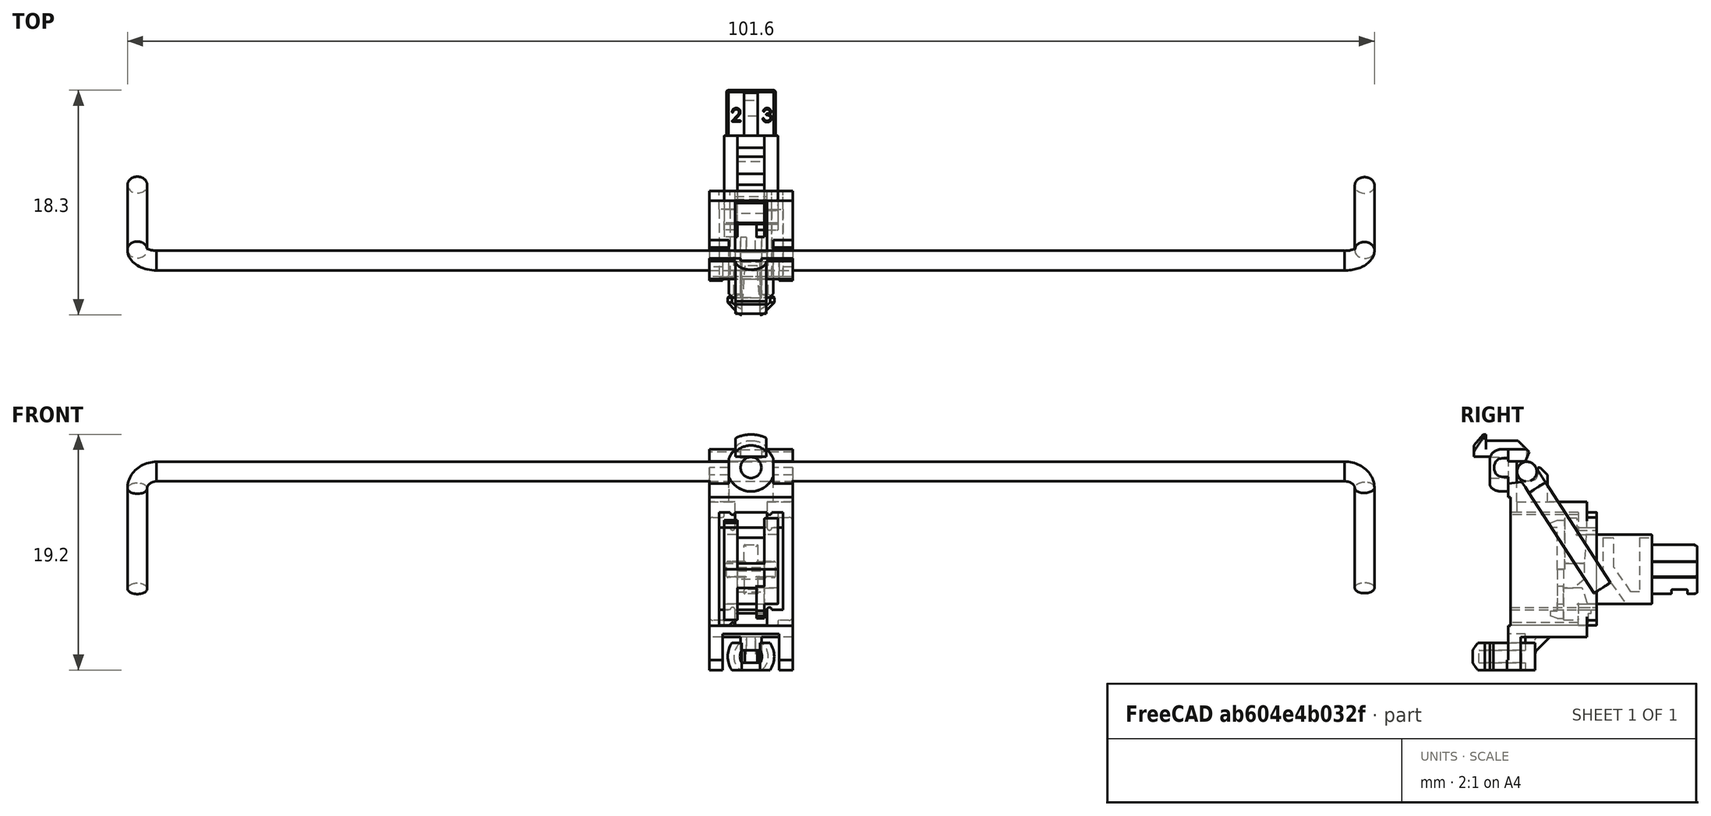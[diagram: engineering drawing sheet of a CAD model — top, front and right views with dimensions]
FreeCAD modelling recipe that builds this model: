
FCSTD DOCUMENT  (FreeCAD 0.18R16158 (Git))
Label: Stabilizer_Cherry_MX_6.25u
License: CreativeCommons Attribution-ShareAlike
LicenseURL: http://creativecommons.org/licenses/by-sa/4.0/
objects: Part::Feature×4, App::Part×3, PartDesign::Plane×2, Sketcher::SketchObject×2, PartDesign::AdditivePipe×1, PartDesign::Body×1
note: 11 computed .brp shape members not serialized (recipe doc carries the construction recipe); baked Part::Feature solids carry a one-line shape summary decoded from their .brp

FEATURE [Part::Feature] Part__Feature  label="Stabilizer_Base"
  shape: bbox 6.802 x 10.1 x 19.67 mm, 163 faces (baked)
FEATURE [Part::Feature] Part__Feature001  label="Stabilizer_Key"
  Placement = pos=(0,8.1,0) rot=(0,0,1;0rad)
  shape: bbox 4.6 x 11.96 x 8.302 mm, 299 faces (baked)
FEATURE [App::Part] Part  label="Stabilizer_End_1"
  Group = -> [Part__Feature001,Part__Feature]
  Origin = -> Origin001
  Placement = pos=(-50,0,0) rot=(0,0,1;0rad)
FEATURE [PartDesign::Plane] DatumPlane
  Length = 112.187
  MapMode = 13
  Placement = pos=(23.0333,0.289849,4.3056) rot=(1,0,0;2.14498rad)
  ResizeMode = 0
  Width = 38.2565
FEATURE [PartDesign::Plane] DatumPlane001
  Length = 38.2565
  MapMode = 11
  Placement = pos=(8e-15,4.09188,-1.57187) rot=(0.272451,-0.272451,0.92279;1.65106rad)
  ResizeMode = 0
  Width = 112.187
FEATURE [Sketcher::SketchObject] Sketch
  MapMode = 5
  Placement = pos=(8e-15,4.09188,-1.57187) rot=(0.272451,-0.272451,0.92279;1.65106rad)
  Support = -> [DatumPlane001]
  sketch-geometry (5):
    g0: Circle CenterX=0 CenterY=50 CenterZ=0 NormalX=0 NormalY=0 NormalZ=1 AngleXU=0 Radius=0.8
    g1: Circle [constr] CenterX=0 CenterY=-50 CenterZ=0 NormalX=0 NormalY=0 NormalZ=1 AngleXU=0 Radius=0.8
    g2: LineSegment [constr] StartX=0 StartY=50 StartZ=0 EndX=0 EndY=0 EndZ=0
    g3: LineSegment [constr] StartX=0 StartY=0 StartZ=0 EndX=0 EndY=-50 EndZ=0
    g4: GeomPoint X=0 Y=-50 Z=0
  constraints (11):
    c: Diameter(g0) = 1.6
    c: PointOnObject(g0,g-2)
    c: PointOnObject(g1,g-2)
    c: Coincident(g2,g0)
    c: Coincident(g2,g-1)
    c: Coincident(g3,g-1)
    c: Coincident(g3,g1)
    c: Equal(g3,g2)
    c: Distance(g2) = 50
    c: Equal(g1,g0)
    c: Coincident(g4,g1)
FEATURE [Sketcher::SketchObject] Sketch001
  ExternalGeometry = -> [Sketch]
  MapMode = 5
  Placement = pos=(23.0333,0.289849,4.3056) rot=(1,0,0;2.14498rad)
  Support = -> [DatumPlane]
  sketch-geometry (5):
    g0: LineSegment StartX=-72.2343 StartY=-6.96088 StartZ=0 EndX=-72.2343 EndY=2.76912 EndZ=0
    g1: LineSegment StartX=-71.4343 StartY=3.56912 StartZ=0 EndX=25.3657 EndY=3.56912 EndZ=0
    g2: LineSegment StartX=26.1657 StartY=2.76912 StartZ=0 EndX=26.1657 EndY=-6.96088 EndZ=0
    g3: ArcOfCircle CenterX=-71.4343 CenterY=2.76912 CenterZ=0 NormalX=0 NormalY=0 NormalZ=1 AngleXU=0 Radius=0.8 StartAngle=1.5708 EndAngle=3.14159
    g4: ArcOfCircle CenterX=25.3657 CenterY=2.76912 CenterZ=0 NormalX=0 NormalY=0 NormalZ=1 AngleXU=0 Radius=0.8 StartAngle=0 EndAngle=1.5708
FEATURE [PartDesign::AdditivePipe] AdditivePipe
  AuxilleryCurvelinear = true
  AuxillerySpineTangent = false
  Binormal = (0,0,0)
  Mode = 0
  Placement = pos=(8e-15,4.09188,-1.57187) rot=(0.272451,-0.272451,0.92279;1.65106rad)
  Profile = -> Sketch
  Spine = -> Sketch001
  SpineTangent = false
  Transformation = 0
  Transition = 0
FEATURE [PartDesign::Body] Body  label="Bar"
  Group = -> [DatumPlane,DatumPlane001,Sketch,Sketch001,AdditivePipe]
  Origin = -> Origin002
  Tip = -> AdditivePipe
FEATURE [Part::Feature] Part__Feature002  label="Stabilizer_Key_"
  Placement = pos=(0,8.1,0) rot=(0,0,1;0rad)
  shape: bbox 4.6 x 11.96 x 8.302 mm, 299 faces (baked)
FEATURE [Part::Feature] Part__Feature003  label="Stabilizer_Base_"
  shape: bbox 6.802 x 10.1 x 19.67 mm, 163 faces (baked)
FEATURE [App::Part] Part001  label="Stabilizer_End_2"
  Group = -> [Part__Feature002,Part__Feature003]
  Origin = -> Origin003
  Placement = pos=(50,0,0) rot=(0,0,1;0rad)
FEATURE [App::Part] Stabilizer___open  label="Stabilizer_Cherry_MX_6.25u"
  Group = -> [Body,Part001,Part]
  Origin = -> Origin
  Placement = pos=(0,8e-16,3.65) rot=(1,0,0;1.5708rad)
